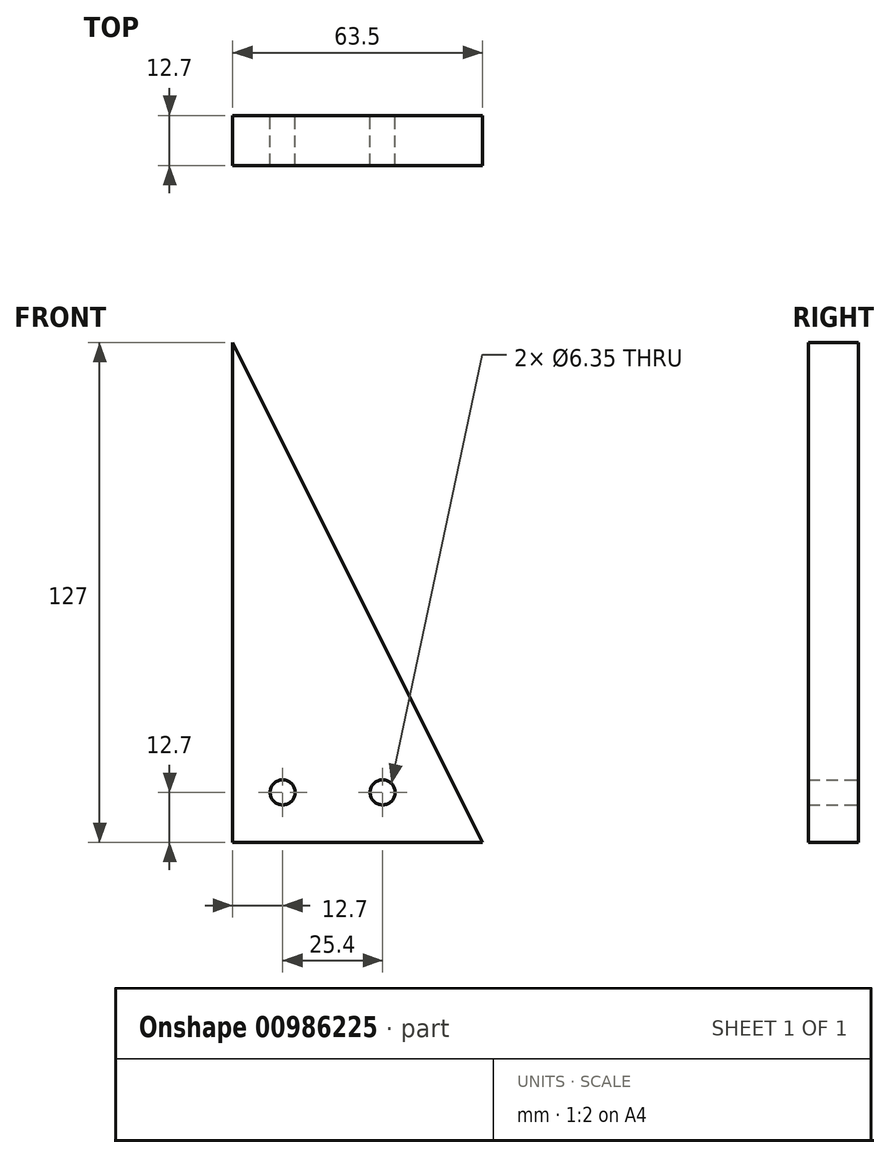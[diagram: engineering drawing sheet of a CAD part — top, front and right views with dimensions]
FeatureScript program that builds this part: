
annotation { "Feature Type Name" : "Feature", "Feature Type Description" : "" }
export const myFeature = defineFeature(function(context is Context, id is Id, definition is map)
    precondition{}
    {
        {
            var Q0;
            Q0=qCreatedBy(makeId("Front.planeOp"),FACE);
            var sketch = newSketch(context, id + "F0", { "sketchPlane" : qUnion([Q0])});
            skLineSegment(sketch, "E0", {"start": v(0, 0) * mm, "end": v(0, 127) * mm});
            skLineSegment(sketch, "E1", {"start": v(0, 127) * mm, "end": v(63.5, 0) * mm});
            skLineSegment(sketch, "E2", {"start": v(63.5, 0) * mm, "end": v(0, 0) * mm});
            skCircle(sketch, "E3", {"center": v(12.7, 12.7) * mm, "radius": 3.18 * mm});
            skCircle(sketch, "E4", {"center": v(38.1, 12.7) * mm, "radius": 3.18 * mm});
            skSolve(sketch);
        }
        {
            var Q0;
            Q0=makeQuery(id+"F0.imprint","IMPRINT",FACE,{"disambiguationData":[TD([[makeQuery(id+"F0.imprint","IMPRINT",EDGE,{"derivedFrom":sQuery(id+"F0.wireOp",EDGE,"E0")}),-1.0]])]});
            extrude(context, id + "F1", {"entities" : qUnion([Q0]), "depth" : 12.7 * mm, "offsetDistance" : 25.4 * mm});
        }
    });
